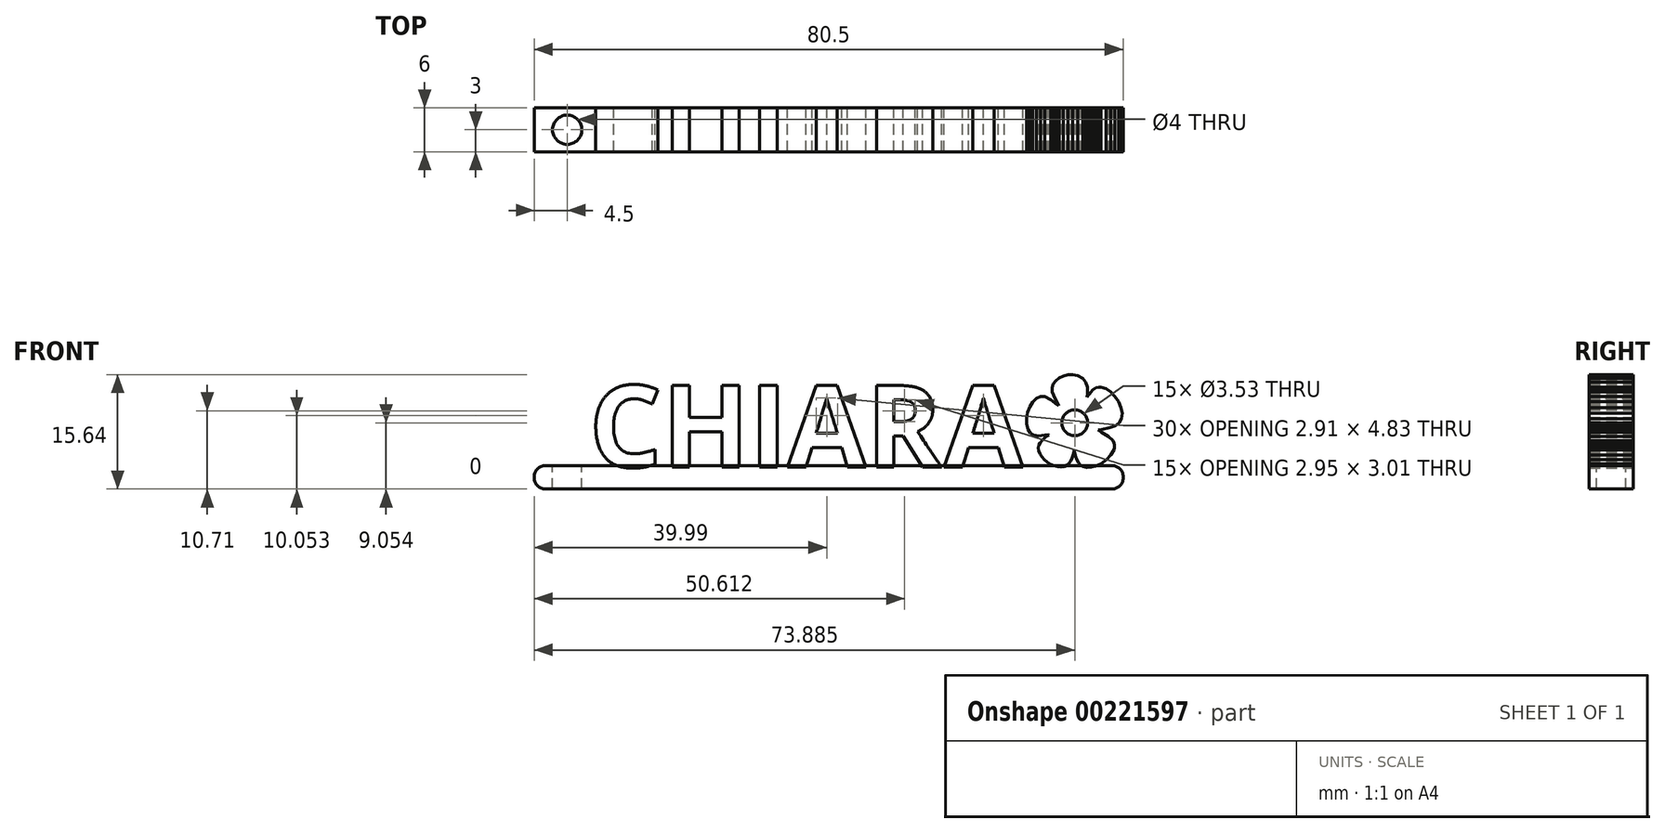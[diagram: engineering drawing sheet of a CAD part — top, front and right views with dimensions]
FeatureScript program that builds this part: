
annotation { "Feature Type Name" : "Feature", "Feature Type Description" : "" }
export const myFeature = defineFeature(function(context is Context, id is Id, definition is map)
    precondition{}
    {
        {
            var Q0;
            Q0=qCreatedBy(makeId("Front.planeOp"),FACE);
            var sketch = newSketch(context, id + "F0", { "sketchPlane" : qUnion([Q0])});
            skText(sketch, "E0", { "text": "CHIARA", "fontName": "OpenSans-Bold.ttf"});
            skLineSegment(sketch, "E1.0.0", {"start": v(49.2, 0.1) * mm, "end": v(49.97, 0.46) * mm});
            skLineSegment(sketch, "E1.0.1", {"start": v(49.97, 0.46) * mm, "end": v(50.72, 1.02) * mm});
            skLineSegment(sketch, "E1.0.2", {"start": v(50.72, 1.02) * mm, "end": v(51.33, 1.67) * mm});
            skLineSegment(sketch, "E1.0.3", {"start": v(51.33, 1.67) * mm, "end": v(51.72, 2.35) * mm});
            skLineSegment(sketch, "E1.0.4", {"start": v(51.72, 2.35) * mm, "end": v(51.82, 2.7) * mm});
            skLineSegment(sketch, "E1.0.5", {"start": v(51.82, 2.7) * mm, "end": v(51.84, 3.02) * mm});
            skLineSegment(sketch, "E1.0.6", {"start": v(51.84, 3.02) * mm, "end": v(51.77, 3.33) * mm});
            skLineSegment(sketch, "E1.0.7", {"start": v(51.77, 3.33) * mm, "end": v(51.62, 3.62) * mm});
            skLineSegment(sketch, "E1.0.8", {"start": v(51.62, 3.62) * mm, "end": v(51.02, 4.2) * mm});
            skLineSegment(sketch, "E1.0.9", {"start": v(51.02, 4.2) * mm, "end": v(50.01, 4.79) * mm});
            skLineSegment(sketch, "E1.0.10", {"start": v(50.01, 4.79) * mm, "end": v(49.58, 5.06) * mm});
            skLineSegment(sketch, "E1.0.11", {"start": v(49.58, 5.06) * mm, "end": v(50.09, 5.16) * mm});
            skLineSegment(sketch, "E1.0.12", {"start": v(50.09, 5.16) * mm, "end": v(51.2, 5.37) * mm});
            skLineSegment(sketch, "E1.0.13", {"start": v(51.2, 5.37) * mm, "end": v(51.96, 5.65) * mm});
            skLineSegment(sketch, "E1.0.14", {"start": v(51.96, 5.65) * mm, "end": v(52.45, 6.04) * mm});
            skLineSegment(sketch, "E1.0.15", {"start": v(52.45, 6.04) * mm, "end": v(52.75, 6.58) * mm});
            skLineSegment(sketch, "E1.0.16", {"start": v(52.75, 6.58) * mm, "end": v(52.86, 7.33) * mm});
            skLineSegment(sketch, "E1.0.17", {"start": v(52.86, 7.33) * mm, "end": v(52.73, 8.14) * mm});
            skLineSegment(sketch, "E1.0.18", {"start": v(52.73, 8.14) * mm, "end": v(52.4, 8.93) * mm});
            skLineSegment(sketch, "E1.0.19", {"start": v(52.4, 8.93) * mm, "end": v(51.9, 9.67) * mm});
            skLineSegment(sketch, "E1.0.20", {"start": v(51.9, 9.67) * mm, "end": v(51.3, 10.28) * mm});
            skLineSegment(sketch, "E1.0.21", {"start": v(51.3, 10.28) * mm, "end": v(50.64, 10.72) * mm});
            skLineSegment(sketch, "E1.0.22", {"start": v(50.64, 10.72) * mm, "end": v(49.96, 10.93) * mm});
            skLineSegment(sketch, "E1.0.23", {"start": v(49.96, 10.93) * mm, "end": v(49.62, 10.93) * mm});
            skLineSegment(sketch, "E1.0.24", {"start": v(49.62, 10.93) * mm, "end": v(49.3, 10.85) * mm});
            skLineSegment(sketch, "E1.0.25", {"start": v(49.3, 10.85) * mm, "end": v(48.86, 10.56) * mm});
            skLineSegment(sketch, "E1.0.26", {"start": v(48.86, 10.56) * mm, "end": v(48.36, 9.98) * mm});
            skLineSegment(sketch, "E1.0.27", {"start": v(48.36, 9.98) * mm, "end": v(48.05, 9.58) * mm});
            skLineSegment(sketch, "E1.0.28", {"start": v(48.05, 9.58) * mm, "end": v(48.1, 10.03) * mm});
            skLineSegment(sketch, "E1.0.29", {"start": v(48.1, 10.03) * mm, "end": v(48.11, 10.93) * mm});
            skLineSegment(sketch, "E1.0.30", {"start": v(48.11, 10.93) * mm, "end": v(47.9, 11.63) * mm});
            skLineSegment(sketch, "E1.0.31", {"start": v(47.9, 11.63) * mm, "end": v(47.47, 12.15) * mm});
            skLineSegment(sketch, "E1.0.32", {"start": v(47.47, 12.15) * mm, "end": v(46.79, 12.5) * mm});
            skLineSegment(sketch, "E1.0.33", {"start": v(46.79, 12.5) * mm, "end": v(46.1, 12.64) * mm});
            skLineSegment(sketch, "E1.0.34", {"start": v(46.1, 12.64) * mm, "end": v(45.43, 12.62) * mm});
            skLineSegment(sketch, "E1.0.35", {"start": v(45.43, 12.62) * mm, "end": v(44.8, 12.47) * mm});
            skLineSegment(sketch, "E1.0.36", {"start": v(44.8, 12.47) * mm, "end": v(44.24, 12.2) * mm});
            skLineSegment(sketch, "E1.0.37", {"start": v(44.24, 12.2) * mm, "end": v(43.78, 11.83) * mm});
            skLineSegment(sketch, "E1.0.38", {"start": v(43.78, 11.83) * mm, "end": v(43.45, 11.38) * mm});
            skLineSegment(sketch, "E1.0.39", {"start": v(43.45, 11.38) * mm, "end": v(43.28, 10.87) * mm});
            skLineSegment(sketch, "E1.0.40", {"start": v(43.28, 10.87) * mm, "end": v(43.3, 10.3) * mm});
            skLineSegment(sketch, "E1.0.41", {"start": v(43.3, 10.3) * mm, "end": v(43.68, 9.4) * mm});
            skLineSegment(sketch, "E1.0.42", {"start": v(43.68, 9.4) * mm, "end": v(44.15, 8.55) * mm});
            skLineSegment(sketch, "E1.0.43", {"start": v(44.15, 8.55) * mm, "end": v(44.21, 8.4) * mm});
            skLineSegment(sketch, "E1.0.44", {"start": v(44.21, 8.4) * mm, "end": v(44.02, 8.53) * mm});
            skLineSegment(sketch, "E1.0.45", {"start": v(44.02, 8.53) * mm, "end": v(43.1, 9.23) * mm});
            skLineSegment(sketch, "E1.0.46", {"start": v(43.1, 9.23) * mm, "end": v(42.29, 9.63) * mm});
            skLineSegment(sketch, "E1.0.47", {"start": v(42.29, 9.63) * mm, "end": v(41.7, 9.63) * mm});
            skLineSegment(sketch, "E1.0.48", {"start": v(41.7, 9.63) * mm, "end": v(41.15, 9.37) * mm});
            skLineSegment(sketch, "E1.0.49", {"start": v(41.15, 9.37) * mm, "end": v(40.65, 8.9) * mm});
            skLineSegment(sketch, "E1.0.50", {"start": v(40.65, 8.9) * mm, "end": v(40.24, 8.26) * mm});
            skLineSegment(sketch, "E1.0.51", {"start": v(40.24, 8.26) * mm, "end": v(39.94, 7.51) * mm});
            skLineSegment(sketch, "E1.0.52", {"start": v(39.94, 7.51) * mm, "end": v(39.78, 6.71) * mm});
            skLineSegment(sketch, "E1.0.53", {"start": v(39.78, 6.71) * mm, "end": v(39.79, 5.9) * mm});
            skLineSegment(sketch, "E1.0.54", {"start": v(39.79, 5.9) * mm, "end": v(39.99, 5.16) * mm});
            skLineSegment(sketch, "E1.0.55", {"start": v(39.99, 5.16) * mm, "end": v(40.3, 4.64) * mm});
            skLineSegment(sketch, "E1.0.56", {"start": v(40.3, 4.64) * mm, "end": v(40.75, 4.36) * mm});
            skLineSegment(sketch, "E1.0.57", {"start": v(40.75, 4.36) * mm, "end": v(41.4, 4.27) * mm});
            skLineSegment(sketch, "E1.0.58", {"start": v(41.4, 4.27) * mm, "end": v(42.3, 4.37) * mm});
            skLineSegment(sketch, "E1.0.59", {"start": v(42.3, 4.37) * mm, "end": v(42.8, 4.43) * mm});
            skLineSegment(sketch, "E1.0.60", {"start": v(42.8, 4.43) * mm, "end": v(42.83, 4.4) * mm});
            skLineSegment(sketch, "E1.0.61", {"start": v(42.83, 4.4) * mm, "end": v(42.72, 4.33) * mm});
            skLineSegment(sketch, "E1.0.62", {"start": v(42.72, 4.33) * mm, "end": v(42.34, 4.07) * mm});
            skLineSegment(sketch, "E1.0.63", {"start": v(42.34, 4.07) * mm, "end": v(41.95, 3.71) * mm});
            skLineSegment(sketch, "E1.0.64", {"start": v(41.95, 3.71) * mm, "end": v(41.64, 3.33) * mm});
            skLineSegment(sketch, "E1.0.65", {"start": v(41.64, 3.33) * mm, "end": v(41.47, 3) * mm});
            skLineSegment(sketch, "E1.0.66", {"start": v(41.47, 3) * mm, "end": v(41.42, 2.6) * mm});
            skLineSegment(sketch, "E1.0.67", {"start": v(41.42, 2.6) * mm, "end": v(41.48, 2.2) * mm});
            skLineSegment(sketch, "E1.0.68", {"start": v(41.48, 2.2) * mm, "end": v(41.64, 1.78) * mm});
            skLineSegment(sketch, "E1.0.69", {"start": v(41.64, 1.78) * mm, "end": v(41.88, 1.39) * mm});
            skLineSegment(sketch, "E1.0.70", {"start": v(41.88, 1.39) * mm, "end": v(42.2, 1.02) * mm});
            skLineSegment(sketch, "E1.0.71", {"start": v(42.2, 1.02) * mm, "end": v(42.6, 0.69) * mm});
            skLineSegment(sketch, "E1.0.72", {"start": v(42.6, 0.69) * mm, "end": v(43.05, 0.4) * mm});
            skLineSegment(sketch, "E1.0.73", {"start": v(43.05, 0.4) * mm, "end": v(43.56, 0.2) * mm});
            skLineSegment(sketch, "E1.0.74", {"start": v(43.56, 0.2) * mm, "end": v(44.06, 0.06) * mm});
            skLineSegment(sketch, "E1.0.75", {"start": v(44.06, 0.06) * mm, "end": v(44.52, 0.02) * mm});
            skLineSegment(sketch, "E1.0.76", {"start": v(44.52, 0.02) * mm, "end": v(44.92, 0.08) * mm});
            skLineSegment(sketch, "E1.0.77", {"start": v(44.92, 0.08) * mm, "end": v(45.28, 0.23) * mm});
            skLineSegment(sketch, "E1.0.78", {"start": v(45.28, 0.23) * mm, "end": v(45.58, 0.49) * mm});
            skLineSegment(sketch, "E1.0.79", {"start": v(45.58, 0.49) * mm, "end": v(45.84, 0.84) * mm});
            skLineSegment(sketch, "E1.0.80", {"start": v(45.84, 0.84) * mm, "end": v(46.04, 1.28) * mm});
            skLineSegment(sketch, "E1.0.81", {"start": v(46.04, 1.28) * mm, "end": v(46.2, 1.83) * mm});
            skLineSegment(sketch, "E1.0.82", {"start": v(46.2, 1.83) * mm, "end": v(46.32, 2.26) * mm});
            skLineSegment(sketch, "E1.0.83", {"start": v(46.32, 2.26) * mm, "end": v(46.37, 2.1) * mm});
            skLineSegment(sketch, "E1.0.84", {"start": v(46.37, 2.1) * mm, "end": v(46.5, 1.53) * mm});
            skLineSegment(sketch, "E1.0.85", {"start": v(46.5, 1.53) * mm, "end": v(46.68, 1) * mm});
            skLineSegment(sketch, "E1.0.86", {"start": v(46.68, 1) * mm, "end": v(46.9, 0.55) * mm});
            skLineSegment(sketch, "E1.0.87", {"start": v(46.9, 0.55) * mm, "end": v(47.15, 0.26) * mm});
            skLineSegment(sketch, "E1.0.88", {"start": v(47.15, 0.26) * mm, "end": v(47.55, 0.05) * mm});
            skLineSegment(sketch, "E1.0.89", {"start": v(47.55, 0.05) * mm, "end": v(48.05, -0.04) * mm});
            skLineSegment(sketch, "E1.0.90", {"start": v(48.05, -0.04) * mm, "end": v(48.6, -0.03) * mm});
            skLineSegment(sketch, "E1.0.91", {"start": v(48.6, -0.03) * mm, "end": v(49.2, 0.1) * mm});
            skCircle(sketch, "E2", {"center": v(46.39, 6.05) * mm, "radius": 1.77 * mm});
            const initialGuessF0  = {"E0": [-0.02, 0, 1, 0, 0.01125]};
            skSetInitialGuess(sketch, initialGuessF0);
            skSolve(sketch);
        }
        {
            var Q0;
            Q0=qSketchRegion(id+"F0",true);
            extrude(context, id + "F1", {"entities" : qUnion([Q0]), "endBound" : BoundingType.SYMMETRIC, "depth" : 6 * mm});
        }
        {
            var Q0;
            Q0=qCreatedBy(makeId("Top.planeOp"),FACE);
            var sketch = newSketch(context, id + "F2", { "sketchPlane" : qUnion([Q0])});
            skLineSegment(sketch, "E3.bottom", {"start": v(-20, 3) * mm, "end": v(53, 3) * mm});
            skLineSegment(sketch, "E3.top", {"start": v(-20, -3) * mm, "end": v(53, -3) * mm});
            skLineSegment(sketch, "E3.left", {"start": v(-20, 3) * mm, "end": v(-20, -3) * mm});
            skLineSegment(sketch, "E3.right", {"start": v(53, 3) * mm, "end": v(53, -3) * mm});
            skSolve(sketch);
        }
        {
            var Q0;
            Q0=makeQuery(id+"F2.imprint","IMPRINT",FACE,{"disambiguationData":[TD([[makeQuery(id+"F2.imprint","IMPRINT",EDGE,{"derivedFrom":sQuery(id+"F2.wireOp",EDGE,"E3.bottom")}),-1.0]])]});
            extrude(context, id + "F3", {"entities" : qUnion([Q0]), "depth" : 0.2 * mm});
        }
        {
            var Q0;
            Q0=makeQuery(id+"F3.opExtrude","CAP_FACE",FACE,{"disambiguationData":[OSD([sQuery(id+"F2.wireOp",EDGE,"E3.bottom"),sQuery(id+"F2.wireOp",EDGE,"E3.top"),sQuery(id+"F2.wireOp",EDGE,"E3.left"),sQuery(id+"F2.wireOp",EDGE,"E3.right")])],"isStart":true});
            extrude(context, id + "F4", {"entities" : qUnion([Q0]), "depth" : 3 * mm});
        }
        {
            var Q0;
            {var subQ0=sQuery(id+"F2.wireOp",EDGE,"E3.left");Q0=makeQuery(id+"FaVoHrOpcFZXiYX_6.opBoolean","MERGE",FACE,{"derivedFrom":[makeQuery(id+"F3.opExtrude","SWEPT_FACE",FACE,{"disambiguationData":[OSD([subQ0])]}),makeQuery(id+"F4.opExtrude","SWEPT_FACE",FACE,{"disambiguationData":[OSD([subQ0])]})]});}
            var sketch = newSketch(context, id + "F5", { "sketchPlane" : qUnion([Q0])});
            skLineSegment(sketch, "E4.bottom", {"start": v(-3, -3) * mm, "end": v(3, -3) * mm});
            skLineSegment(sketch, "E4.top", {"start": v(-3, 0.2) * mm, "end": v(3, 0.2) * mm});
            skLineSegment(sketch, "E4.left", {"start": v(-3, -3) * mm, "end": v(-3, 0.2) * mm});
            skLineSegment(sketch, "E4.right", {"start": v(3, -3) * mm, "end": v(3, 0.2) * mm});
            skSolve(sketch);
        }
        {
            var Q0;
            Q0=qSketchRegion(id+"F5",true);
            extrude(context, id + "F6", {"entities" : qUnion([Q0]), "operationType" : NewBodyOperationType.ADD, "depth" : 7.5 * mm});
        }
        {
            var Q0;
            Q0=makeQuery(id+"F6.opExtrude","CAP_EDGE",EDGE,{"disambiguationData":[OSD([sQuery(id+"F5.wireOp",EDGE,"E4.bottom")])],"isStart":false});
            var Q1;
            Q1=makeQuery(id+"F6.opExtrude","CAP_EDGE",EDGE,{"disambiguationData":[OSD([sQuery(id+"F5.wireOp",EDGE,"E4.top")])],"isStart":false});
            var Q2;
            Q2=makeQuery(id+"F4.opExtrude","CAP_EDGE",EDGE,{"disambiguationData":[OSD([sQuery(id+"F2.wireOp",EDGE,"E3.right")])],"isStart":false});
            fillet(context, id + "F7", {"entities" : qUnion([Q0, Q1, Q2]), "radius" : 1.5 * mm, "tangentPropagation" : true, "allowEdgeOverflow" : false});
        }
        {
            var Q0;
            {var subQ19=sQuery(id+"F2.wireOp",EDGE,"E3.top");var subQ20=sQuery(id+"F2.wireOp",EDGE,"E3.bottom");var subQ63=sQuery(id+"F0.wireOp",EDGE,"E0.sketch_text.stroke-2");var subQ66=sQuery(id+"F2.wireOp",EDGE,"E3.left");Q0=makeQuery(id+"F6.boolean.opBoolean","MERGE",FACE,{"derivedFrom":[makeQuery(id+"FaVoHrOpcFZXiYX_6.opBoolean","SPLIT",FACE,{"disambiguationData":[TD([makeQuery(id+"F1.opExtrude","SWEPT_FACE",FACE,{"disambiguationData":[OSD([subQ63])]})])],"derivedFrom":makeQuery(id+"F3.opExtrude","CAP_FACE",FACE,{"disambiguationData":[OSD([subQ20,subQ19,subQ66,sQuery(id+"F2.wireOp",EDGE,"E3.right")])],"isStart":false})}),makeQuery(id+"F6.opExtrude","SWEPT_FACE",FACE,{"disambiguationData":[OSD([sQuery(id+"F5.wireOp",EDGE,"E4.top")])]})]});}
            var sketch = newSketch(context, id + "F8", { "sketchPlane" : qUnion([Q0])});
            skCircle(sketch, "E5", {"center": v(-23, 0) * mm, "radius": 2 * mm});
            skSolve(sketch);
        }
        {
            var Q0;
            Q0=makeQuery(id+"F8.imprint","IMPRINT",FACE,{"disambiguationData":[TD([[makeQuery(id+"F8.imprint","IMPRINT",EDGE,{"derivedFrom":sQuery(id+"F8.wireOp",EDGE,"E5")}),1.0]])]});
            extrude(context, id + "F9", {"entities" : qUnion([Q0]), "operationType" : NewBodyOperationType.REMOVE, "oppositeDirection" : true, "depth" : 4 * mm});
        }
        {
            var Q0;
            Q0=makeQuery(id+"F3.opExtrude","CAP_EDGE",EDGE,{"disambiguationData":[OSD([sQuery(id+"F2.wireOp",EDGE,"E3.right")])],"isStart":false});
            fillet(context, id + "F10", {"entities" : qUnion([Q0]), "radius" : 1.5 * mm, "tangentPropagation" : true, "allowEdgeOverflow" : false});
        }
    });
